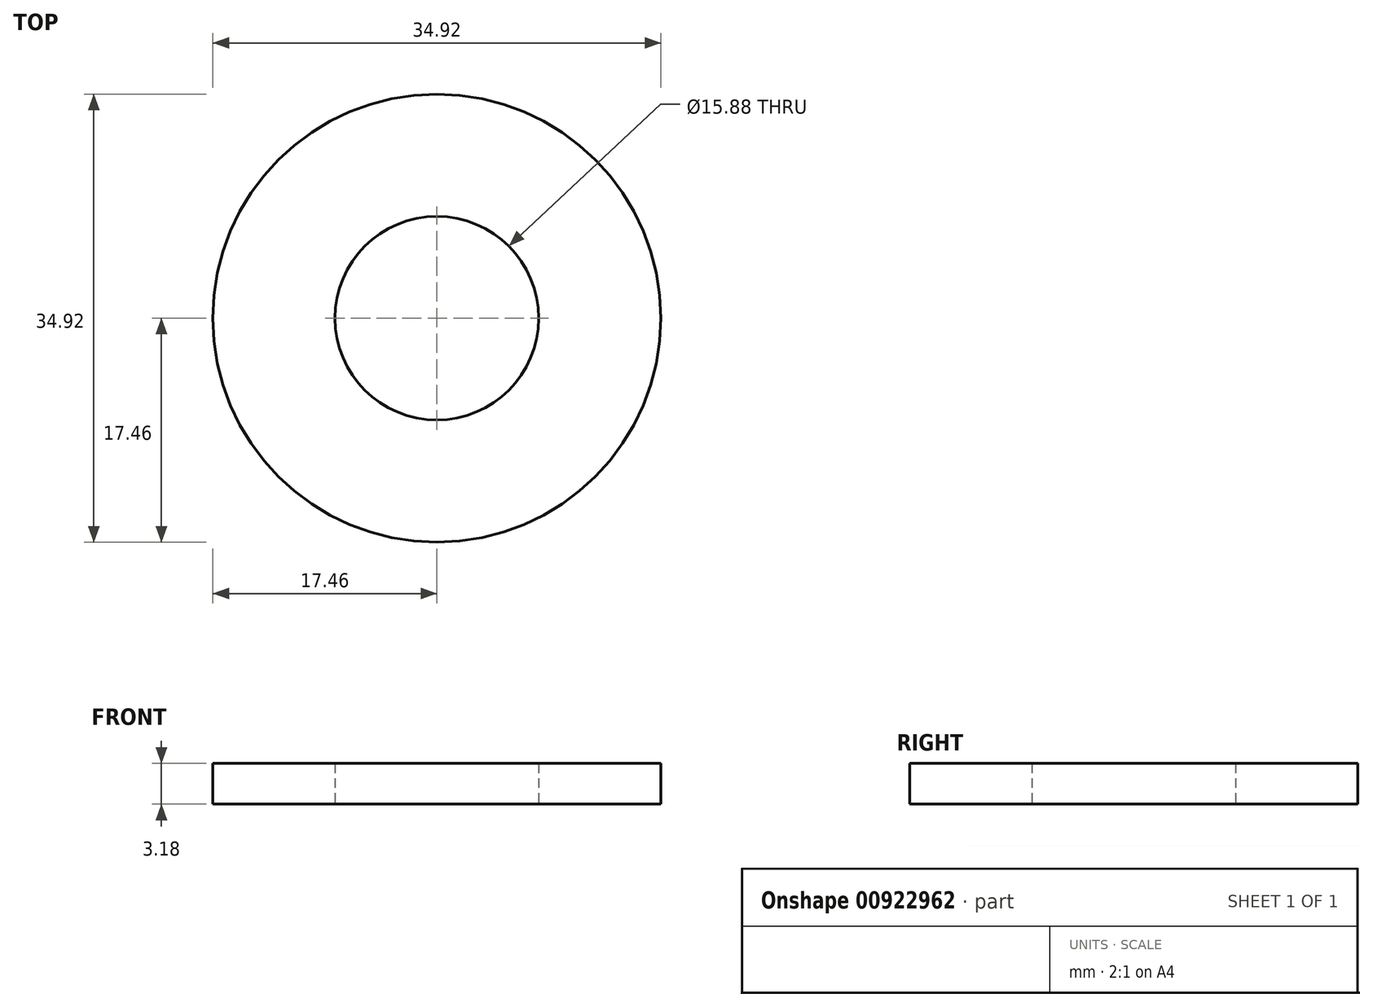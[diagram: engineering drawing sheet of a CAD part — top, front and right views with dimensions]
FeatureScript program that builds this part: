
annotation { "Feature Type Name" : "Feature", "Feature Type Description" : "" }
export const myFeature = defineFeature(function(context is Context, id is Id, definition is map)
    precondition{}
    {
        {
            var Q0;
            Q0=qCreatedBy(makeId("Front.planeOp"),FACE);
            var sketch = newSketch(context, id + "F0", { "sketchPlane" : qUnion([Q0])});
            skLineSegment(sketch, "E0", {"start": v(0, 0) * mm, "end": v(0, 24.58) * mm, "construction": true});
            skLineSegment(sketch, "E1.bottom", {"start": v(-17.46, 3.18) * mm, "end": v(-7.94, 3.18) * mm});
            skLineSegment(sketch, "E1.top", {"start": v(-17.46, 0) * mm, "end": v(-7.94, 0) * mm});
            skLineSegment(sketch, "E1.left", {"start": v(-17.46, 3.18) * mm, "end": v(-17.46, 0) * mm});
            skLineSegment(sketch, "E1.right", {"start": v(-7.94, 3.18) * mm, "end": v(-7.94, 0) * mm});
            skSolve(sketch);
        }
        {
            var Q0;
            Q0 = qSketchRegion(id + "F0", true);
            var Q1;
            Q1=sQuery(id+"F0.wireOp",EDGE,"E0");
            revolve(context, id + "F1", {"surfaceOperationType" : NewSurfaceOperationType.NEW, "entities" : qUnion([Q0]), "axis" : qUnion([Q1]), "revolveType" : RevolveType.FULL});
        }
    });
